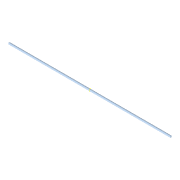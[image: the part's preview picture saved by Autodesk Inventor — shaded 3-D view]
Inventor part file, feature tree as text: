
AUTODESK INVENTOR PART (.ipt)
format: ipt  version: 2022 (Build 260153000, 153)  size: 76,800 bytes
history: native  units: mm
features: extrude x1, plane x1, sketch x1
ambient origin geometry x8: Origin, YZ Plane, XZ Plane, XY Plane, X Axis, Y Axis, Z Axis, Center Point
bodies: Solid1 (feature_tree)
feature tree (3):
  extrude  "Extrusion1"  Depth=200.0mm
  plane  "Work Plane1"
  sketch  "Sketch1"  dims[d0=2.2mm d1=0.5mm d2=200.0mm d3=0.0mm]
